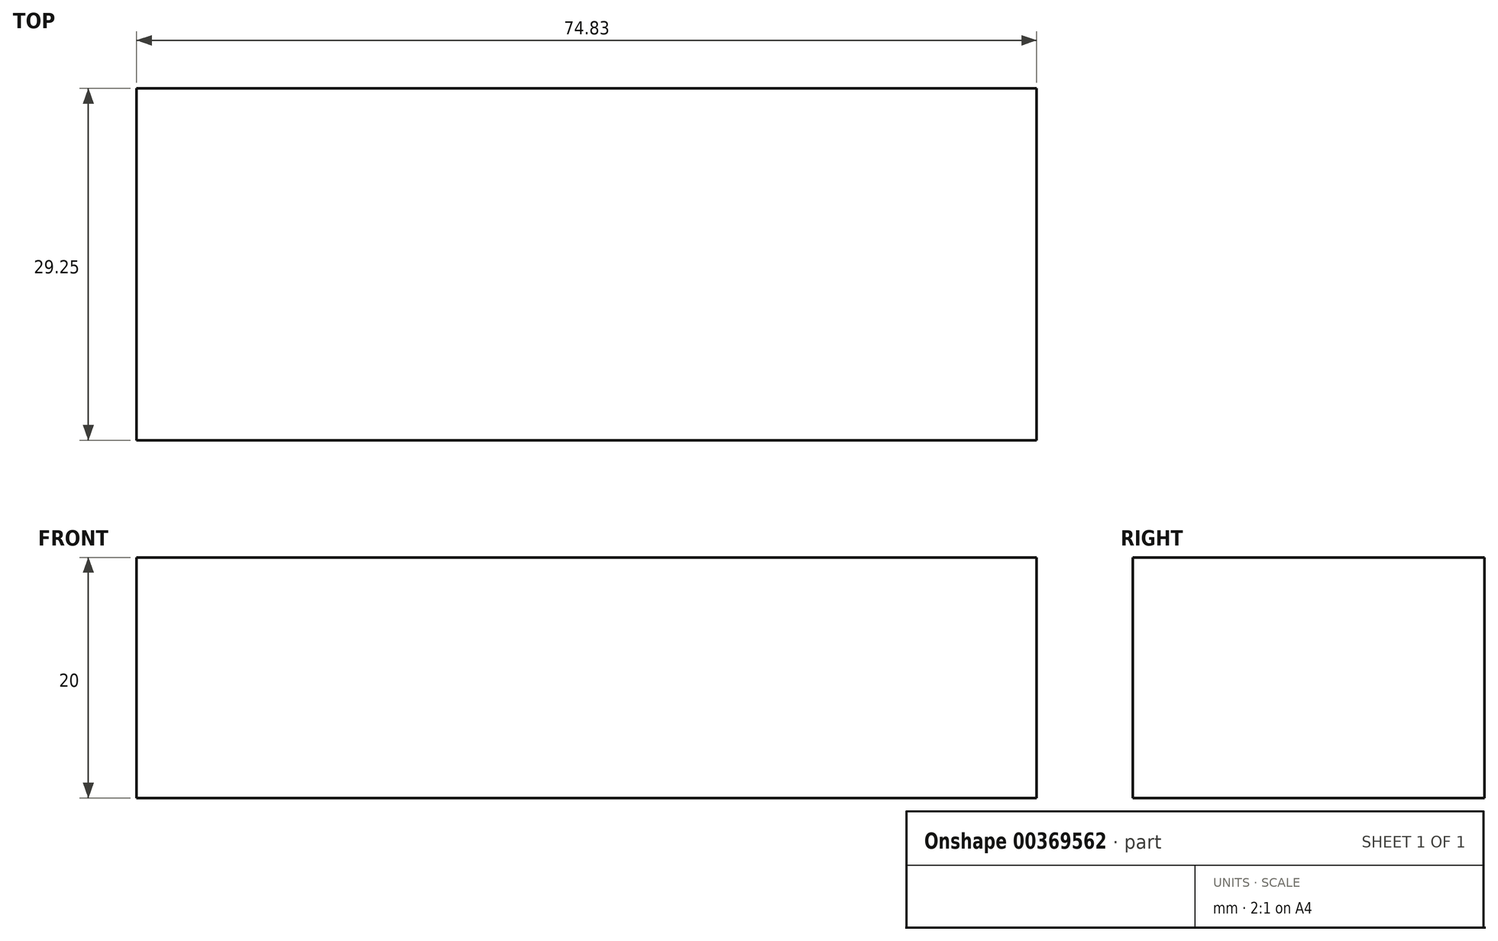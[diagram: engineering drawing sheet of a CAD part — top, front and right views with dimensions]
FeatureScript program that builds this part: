
annotation { "Feature Type Name" : "Feature", "Feature Type Description" : "" }
export const myFeature = defineFeature(function(context is Context, id is Id, definition is map)
    precondition{}
    {
        {
            var Q0;
            Q0=qCreatedBy(makeId("Top.planeOp"),FACE);
            var sketch = newSketch(context, id + "F0", { "sketchPlane" : qUnion([Q0])});
            skLineSegment(sketch, "E0.bottom", {"start": v(-30.45, 17.71) * mm, "end": v(44.38, 17.71) * mm});
            skLineSegment(sketch, "E0.top", {"start": v(-30.45, -11.54) * mm, "end": v(44.38, -11.54) * mm});
            skLineSegment(sketch, "E0.left", {"start": v(-30.45, 17.71) * mm, "end": v(-30.45, -11.54) * mm});
            skLineSegment(sketch, "E0.right", {"start": v(44.38, 17.71) * mm, "end": v(44.38, -11.54) * mm});
            skSolve(sketch);
        }
        {
            var Q0;
            Q0=makeQuery(id+"F0.imprint","IMPRINT",FACE,{"disambiguationData":[TD([[makeQuery(id+"F0.imprint","IMPRINT",EDGE,{"derivedFrom":sQuery(id+"F0.wireOp",EDGE,"E0.bottom")}),-1.0]])]});
            extrude(context, id + "F1", {"entities" : qUnion([Q0]), "depth" : 20 * mm});
        }
    });
